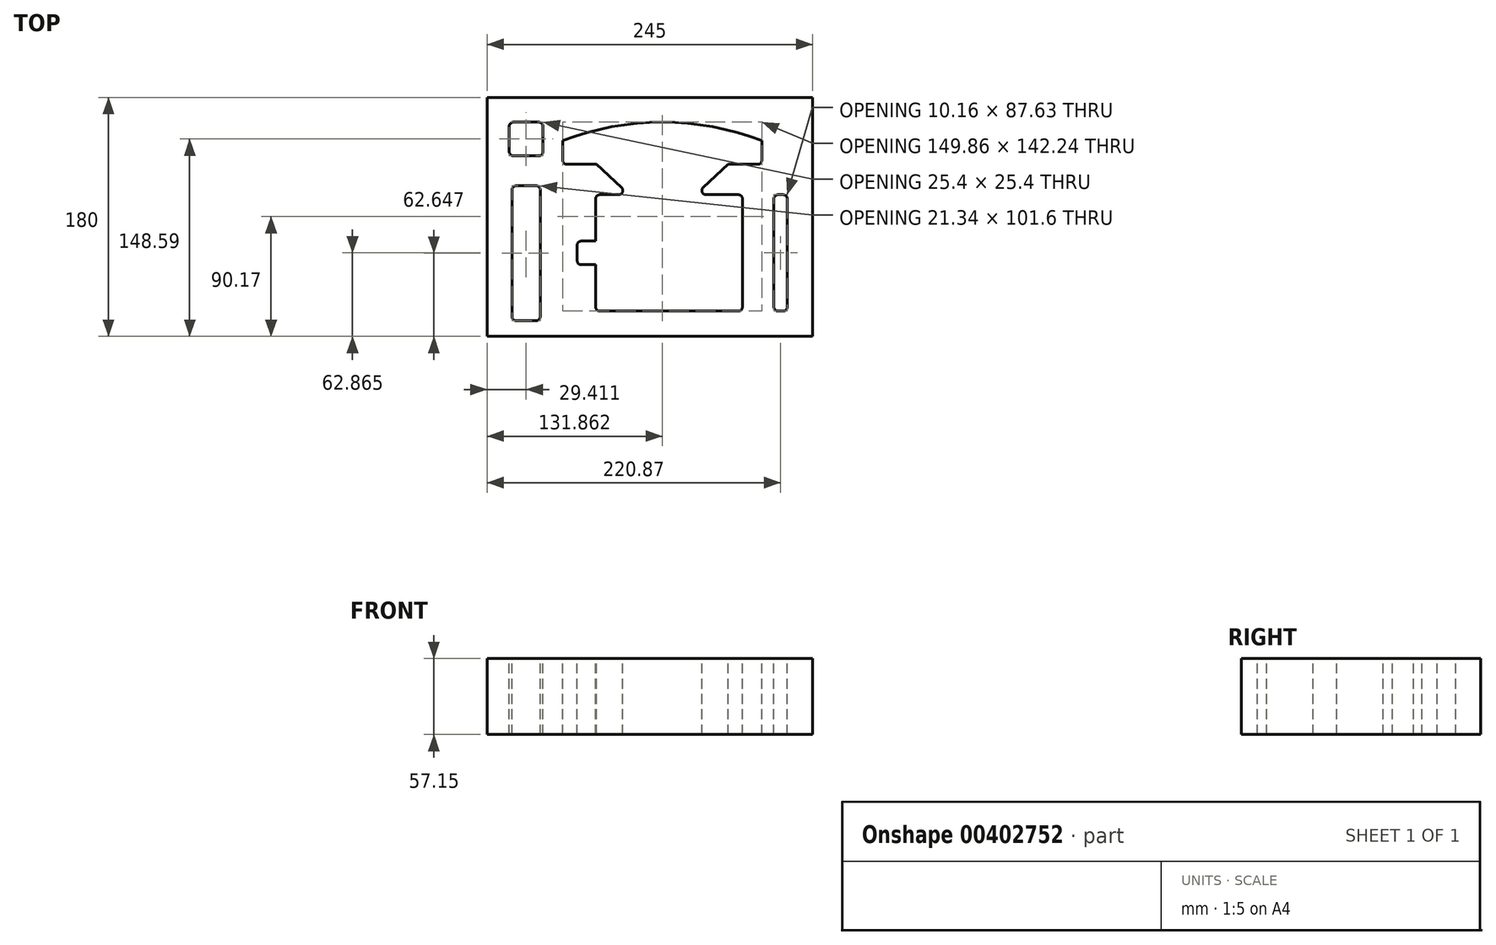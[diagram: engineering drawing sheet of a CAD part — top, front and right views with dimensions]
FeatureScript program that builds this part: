
annotation { "Feature Type Name" : "Feature", "Feature Type Description" : "" }
export const myFeature = defineFeature(function(context is Context, id is Id, definition is map)
    precondition{}
    {
        {
            var Q0;
            Q0=qCreatedBy(makeId("Top.planeOp"),FACE);
            var sketch = newSketch(context, id + "F0", { "sketchPlane" : qUnion([Q0])});
            skLineSegment(sketch, "E0.bottom", {"start": v(-122.5, 90) * mm, "end": v(122.5, 90) * mm});
            skLineSegment(sketch, "E0.top", {"start": v(-122.5, -90) * mm, "end": v(122.5, -90) * mm});
            skLineSegment(sketch, "E0.left", {"start": v(-122.5, 90) * mm, "end": v(-122.5, -90) * mm});
            skLineSegment(sketch, "E0.right", {"start": v(122.5, 90) * mm, "end": v(122.5, -90) * mm});
            skPoint(sketch, "E0.middle", {"position": v(0, 0) * mm});
            skSolve(sketch);
        }
        {
            var Q0;
            Q0 = qSketchRegion(id + "F0", true);
            extrude(context, id + "F1", {"entities" : qUnion([Q0]), "depth" : 57.15 * mm});
        }
        {
            var Q0;
            Q0=makeQuery(id+"F1.opExtrude","CAP_FACE",FACE,{"disambiguationData":[OSD([sQuery(id+"F0.wireOp",EDGE,"E0.bottom"),sQuery(id+"F0.wireOp",EDGE,"E0.top"),sQuery(id+"F0.wireOp",EDGE,"E0.left"),sQuery(id+"F0.wireOp",EDGE,"E0.right")])],"isStart":false});
            var sketch = newSketch(context, id + "F2", { "sketchPlane" : qUnion([Q0])});
            skLineSegment(sketch, "E1.bottom", {"start": v(-102.61, 71.29) * mm, "end": v(-83.56, 71.29) * mm});
            skLineSegment(sketch, "E1.top", {"start": v(-102.61, 45.89) * mm, "end": v(-83.56, 45.89) * mm});
            skLineSegment(sketch, "E1.left", {"start": v(-105.79, 68.11) * mm, "end": v(-105.79, 49.06) * mm});
            skLineSegment(sketch, "E1.right", {"start": v(-80.39, 68.11) * mm, "end": v(-80.39, 49.06) * mm});
            skLineSegment(sketch, "E2", {"start": v(-105.79, 58.59) * mm, "end": v(-122.5, 58.59) * mm, "construction": true});
            skLineSegment(sketch, "E3.bottom", {"start": v(-100.58, 23.45) * mm, "end": v(-85.6, 23.45) * mm});
            skLineSegment(sketch, "E3.top", {"start": v(-100.58, -78.15) * mm, "end": v(-85.6, -78.15) * mm});
            skLineSegment(sketch, "E3.left", {"start": v(-103.76, 20.27) * mm, "end": v(-103.76, -74.98) * mm});
            skLineSegment(sketch, "E3.right", {"start": v(-82.42, 20.27) * mm, "end": v(-82.42, -74.98) * mm});
            skLineSegment(sketch, "E4", {"start": v(-93.09, 23.45) * mm, "end": v(-103.76, -27.35) * mm, "construction": true});
            skLineSegment(sketch, "E5", {"start": v(-101.67, -17.3) * mm, "end": v(-122.5, -17.3) * mm, "construction": true});
            skLineSegment(sketch, "E6.bottom", {"start": v(96.47, 16.68) * mm, "end": v(100.28, 16.68) * mm});
            skLineSegment(sketch, "E6.top", {"start": v(96.47, -70.95) * mm, "end": v(100.28, -70.95) * mm});
            skLineSegment(sketch, "E6.left", {"start": v(93.3, 13.5) * mm, "end": v(93.3, -67.78) * mm});
            skLineSegment(sketch, "E6.right", {"start": v(103.45, 13.5) * mm, "end": v(103.45, -67.78) * mm});
            skLineSegment(sketch, "E7", {"start": v(84.65, -27.14) * mm, "end": v(93.3, -27.14) * mm, "construction": true});
            skLineSegment(sketch, "E8.bottom", {"start": v(-37.63, -70.95) * mm, "end": v(66.51, -70.95) * mm});
            skLineSegment(sketch, "E8.top", {"start": v(-37.63, 16.68) * mm, "end": v(-23.52, 16.68) * mm});
            skLineSegment(sketch, "E8.left", {"start": v(-40.8, -67.77) * mm, "end": v(-40.8, 13.5) * mm});
            skLineSegment(sketch, "E8.right", {"start": v(69.69, -67.77) * mm, "end": v(69.69, 13.5) * mm});
            skLineSegment(sketch, "E9.left", {"start": v(-40.8, -18.24) * mm, "end": v(-40.8, -36.02) * mm});
            skLineSegment(sketch, "E9.right", {"start": v(-54.75, -21.42) * mm, "end": v(-54.75, -32.85) * mm});
            skLineSegment(sketch, "E10", {"start": v(-54.75, -27.13) * mm, "end": v(69.69, -27.13) * mm, "construction": true});
            skPoint(sketch, "E10.endSnap0", {"position": v(69.69, -27.13) * mm});
            skPoint(sketch, "E11.oppositeSnap0", {"position": v(-47.77, -36.02) * mm});
            skLineSegment(sketch, "E11.bottom", {"start": v(-40.8, -13.16) * mm, "end": v(-47.77, -13.16) * mm, "construction": true});
            skLineSegment(sketch, "E11.left", {"start": v(-40.8, -13.16) * mm, "end": v(-40.8, -41.1) * mm});
            skLineSegment(sketch, "E12", {"start": v(-54.75, -27.13) * mm, "end": v(-47.77, -27.13) * mm, "construction": true});
            skLineSegment(sketch, "E13", {"start": v(-54.75, -18.24) * mm, "end": v(-47.77, -13.16) * mm, "construction": true});
            skLineSegment(sketch, "E14", {"start": v(-54.75, -36.02) * mm, "end": v(-47.77, -41.1) * mm, "construction": true});
            skLineSegment(sketch, "E15", {"start": v(-47.77, -41.1) * mm, "end": v(-40.8, -41.1) * mm, "construction": true});
            skLineSegment(sketch, "E16", {"start": v(-15.4, 16.68) * mm, "end": v(-15.4, 39.54) * mm, "construction": true});
            skLineSegment(sketch, "E17", {"start": v(34.13, 16.68) * mm, "end": v(34.13, 39.54) * mm, "construction": true});
            skLineSegment(sketch, "E18.bottom", {"start": v(81.12, 39.54) * mm, "end": v(-62.4, 39.54) * mm});
            skLineSegment(sketch, "E18.top", {"start": v(84.3, 57.32) * mm, "end": v(-65.57, 57.32) * mm});
            skLineSegment(sketch, "E18.left", {"start": v(84.3, 42.72) * mm, "end": v(84.3, 57.32) * mm});
            skLineSegment(sketch, "E18.right", {"start": v(-65.57, 42.72) * mm, "end": v(-65.57, 57.32) * mm});
            skLineSegment(sketch, "E19", {"start": v(-15.4, 39.54) * mm, "end": v(34.13, 16.68) * mm, "construction": true});
            skLineSegment(sketch, "E20", {"start": v(9.36, 28.11) * mm, "end": v(9.36, 57.32) * mm, "construction": true});
            skLineSegment(sketch, "E21", {"start": v(9.36, 57.32) * mm, "end": v(9.36, 71.3) * mm, "construction": true});
            skArc(sketch, "E22", {"start": v(84.3, 57.32) * mm, "mid": v(9.36, 71.3) * mm, "end": v(-65.57, 57.32) * mm});
            skLineSegment(sketch, "E23", {"start": v(-51.57, -18.24) * mm, "end": v(-40.8, -18.24) * mm});
            skLineSegment(sketch, "E24", {"start": v(-51.57, -36.02) * mm, "end": v(-40.8, -36.02) * mm});
            skCircle(sketch, "E25", {"center": v(-149.92, 8.88) * mm, "radius": 12.7 * mm, "construction": true});
            skLineSegment(sketch, "E26", {"start": v(-93.09, 45.89) * mm, "end": v(-93.09, 71.29) * mm, "construction": true});
            skPoint(sketch, "E27.visualSharp", {"position": v(-105.79, 71.29) * mm});
            skArc(sketch, "E27.filletArc", {"start": v(-102.61, 71.29) * mm, "mid": v(-104.86, 70.36) * mm, "end": v(-105.79, 68.11) * mm});
            skPoint(sketch, "E28.visualSharp", {"position": v(-80.39, 71.29) * mm});
            skArc(sketch, "E28.filletArc", {"start": v(-80.39, 68.11) * mm, "mid": v(-81.32, 70.36) * mm, "end": v(-83.56, 71.29) * mm});
            skPoint(sketch, "E29.visualSharp", {"position": v(-80.39, 45.89) * mm});
            skArc(sketch, "E29.filletArc", {"start": v(-83.56, 45.89) * mm, "mid": v(-81.32, 46.82) * mm, "end": v(-80.39, 49.06) * mm});
            skPoint(sketch, "E30.visualSharp", {"position": v(-105.79, 45.89) * mm});
            skArc(sketch, "E30.filletArc", {"start": v(-105.79, 49.06) * mm, "mid": v(-104.86, 46.82) * mm, "end": v(-102.61, 45.89) * mm});
            skPoint(sketch, "E31.visualSharp", {"position": v(-103.76, 23.45) * mm});
            skArc(sketch, "E31.filletArc", {"start": v(-100.58, 23.45) * mm, "mid": v(-102.83, 22.52) * mm, "end": v(-103.76, 20.27) * mm});
            skPoint(sketch, "E32.visualSharp", {"position": v(-82.42, 23.45) * mm});
            skArc(sketch, "E32.filletArc", {"start": v(-82.42, 20.27) * mm, "mid": v(-83.35, 22.52) * mm, "end": v(-85.6, 23.45) * mm});
            skPoint(sketch, "E33.visualSharp", {"position": v(-82.42, -78.15) * mm});
            skArc(sketch, "E33.filletArc", {"start": v(-85.6, -78.15) * mm, "mid": v(-83.35, -77.22) * mm, "end": v(-82.42, -74.98) * mm});
            skPoint(sketch, "E34.visualSharp", {"position": v(-103.76, -78.15) * mm});
            skArc(sketch, "E34.filletArc", {"start": v(-103.76, -74.98) * mm, "mid": v(-102.83, -77.22) * mm, "end": v(-100.58, -78.15) * mm});
            skPoint(sketch, "E35.visualSharp", {"position": v(103.45, -70.95) * mm});
            skArc(sketch, "E35.filletArc", {"start": v(100.28, -70.95) * mm, "mid": v(102.52, -70.02) * mm, "end": v(103.45, -67.78) * mm});
            skPoint(sketch, "E36.visualSharp", {"position": v(93.3, 16.68) * mm});
            skArc(sketch, "E36.filletArc", {"start": v(96.47, 16.68) * mm, "mid": v(94.22, 15.75) * mm, "end": v(93.3, 13.5) * mm});
            skPoint(sketch, "E37.visualSharp", {"position": v(93.3, -70.95) * mm});
            skArc(sketch, "E37.filletArc", {"start": v(93.3, -67.78) * mm, "mid": v(94.22, -70.02) * mm, "end": v(96.47, -70.95) * mm});
            skPoint(sketch, "E38.visualSharp", {"position": v(103.45, 16.68) * mm});
            skArc(sketch, "E38.filletArc", {"start": v(103.45, 13.5) * mm, "mid": v(102.52, 15.75) * mm, "end": v(100.28, 16.68) * mm});
            skPoint(sketch, "E39.visualSharp", {"position": v(69.69, -70.95) * mm});
            skArc(sketch, "E39.filletArc", {"start": v(66.51, -70.95) * mm, "mid": v(68.76, -70.02) * mm, "end": v(69.69, -67.77) * mm});
            skPoint(sketch, "E40.visualSharp", {"position": v(-40.8, -70.95) * mm});
            skArc(sketch, "E40.filletArc", {"start": v(-40.8, -67.77) * mm, "mid": v(-39.87, -70.02) * mm, "end": v(-37.63, -70.95) * mm});
            skPoint(sketch, "E41.visualSharp", {"position": v(-54.75, -18.24) * mm});
            skArc(sketch, "E41.filletArc", {"start": v(-51.57, -18.24) * mm, "mid": v(-53.82, -19.17) * mm, "end": v(-54.75, -21.42) * mm});
            skPoint(sketch, "E42.visualSharp", {"position": v(-54.75, -36.02) * mm});
            skArc(sketch, "E42.filletArc", {"start": v(-54.75, -32.85) * mm, "mid": v(-53.82, -35.1) * mm, "end": v(-51.57, -36.02) * mm});
            skPoint(sketch, "E43.visualSharp", {"position": v(-40.8, 16.68) * mm});
            skArc(sketch, "E43.filletArc", {"start": v(-37.63, 16.68) * mm, "mid": v(-39.87, 15.75) * mm, "end": v(-40.8, 13.5) * mm});
            skLineSegment(sketch, "E44", {"start": v(-21.37, 22.19) * mm, "end": v(-40.17, 39.54) * mm});
            skLineSegment(sketch, "E45", {"start": v(40.1, 22.19) * mm, "end": v(58.9, 39.54) * mm});
            skLineSegment(sketch, "E46", {"start": v(-15.4, 39.54) * mm, "end": v(-40.17, 39.54) * mm, "construction": true});
            skLineSegment(sketch, "E47", {"start": v(34.13, 39.54) * mm, "end": v(58.9, 39.54) * mm, "construction": true});
            skPoint(sketch, "E48.visualSharp", {"position": v(-65.57, 39.54) * mm});
            skArc(sketch, "E48.filletArc", {"start": v(-65.57, 42.72) * mm, "mid": v(-64.64, 40.47) * mm, "end": v(-62.4, 39.54) * mm});
            skPoint(sketch, "E49.visualSharp", {"position": v(84.3, 39.54) * mm});
            skArc(sketch, "E49.filletArc", {"start": v(81.12, 39.54) * mm, "mid": v(83.36, 40.47) * mm, "end": v(84.3, 42.72) * mm});
            skPoint(sketch, "E50.visualSharp", {"position": v(69.69, 16.68) * mm});
            skArc(sketch, "E50.filletArc", {"start": v(69.69, 13.5) * mm, "mid": v(68.76, 15.75) * mm, "end": v(66.51, 16.68) * mm});
            skLineSegment(sketch, "E51.trimOffspring", {"start": v(42.25, 16.68) * mm, "end": v(66.51, 16.68) * mm});
            skPoint(sketch, "E52.end.orphan", {"position": v(-29.37, 39.54) * mm});
            skPoint(sketch, "E53.end.orphan", {"position": v(49.37, 39.54) * mm});
            skPoint(sketch, "E54.visualSharp", {"position": v(-15.4, 16.68) * mm});
            skArc(sketch, "E54.filletArc", {"start": v(-23.52, 16.68) * mm, "mid": v(-20.57, 18.7) * mm, "end": v(-21.37, 22.19) * mm});
            skPoint(sketch, "E55.visualSharp", {"position": v(34.13, 16.68) * mm});
            skArc(sketch, "E55.filletArc", {"start": v(40.1, 22.19) * mm, "mid": v(39.3, 18.7) * mm, "end": v(42.25, 16.68) * mm});
            skSolve(sketch);
        }
        {
            var Q0;
            Q0 = qSketchRegion(id + "F2", true);
            var Q1;
            Q1=makeQuery(id+"F1.opExtrude","CAP_FACE",FACE,{"disambiguationData":[OSD([sQuery(id+"F0.wireOp",EDGE,"E0.bottom"),sQuery(id+"F0.wireOp",EDGE,"E0.top"),sQuery(id+"F0.wireOp",EDGE,"E0.left"),sQuery(id+"F0.wireOp",EDGE,"E0.right")])],"isStart":true});
            extrude(context, id + "F3", {"entities" : qUnion([Q0]), "operationType" : NewBodyOperationType.REMOVE, "endBound" : BoundingType.UP_TO_SURFACE, "oppositeDirection" : true, "endBoundEntityFace" : qUnion([Q1]), "depth" : 25.4 * mm});
        }
    });
